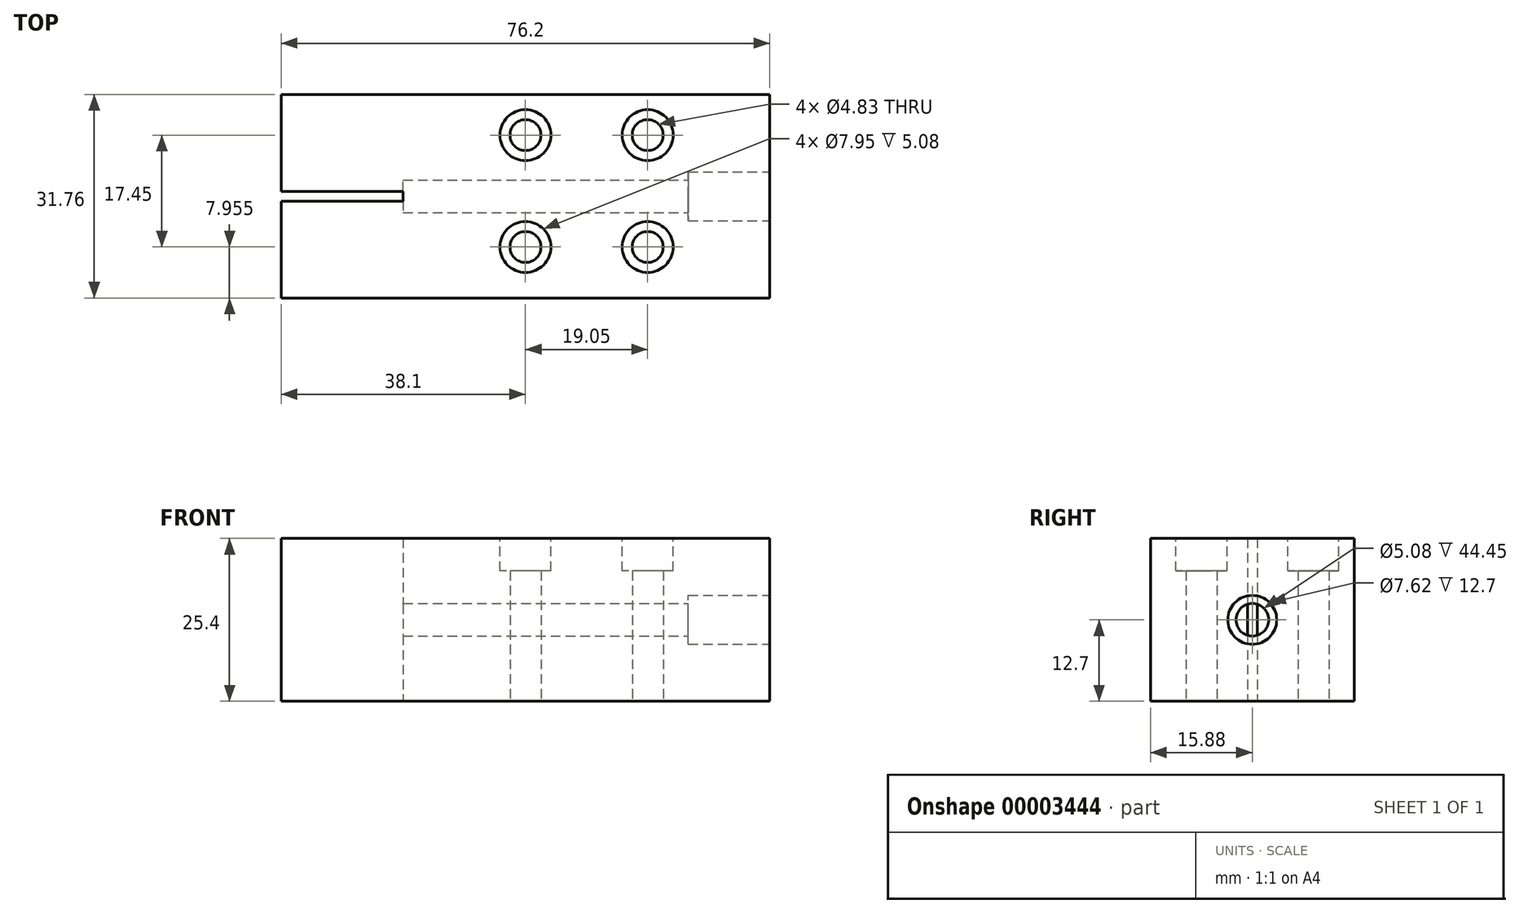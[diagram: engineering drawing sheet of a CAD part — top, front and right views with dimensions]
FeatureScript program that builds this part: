
annotation { "Feature Type Name" : "Feature", "Feature Type Description" : "" }
export const myFeature = defineFeature(function(context is Context, id is Id, definition is map)
    precondition{}
    {
        {
            var Q0;
            Q0=qCreatedBy(makeId("Top.planeOp"),FACE);
            var sketch = newSketch(context, id + "F0", { "sketchPlane" : qUnion([Q0])});
            skLineSegment(sketch, "E0.rect.bottom", {"start": v(-38.1, 15.88) * mm, "end": v(38.1, 15.88) * mm});
            skLineSegment(sketch, "E0.rect.top", {"start": v(-38.1, -15.88) * mm, "end": v(38.1, -15.88) * mm});
            skLineSegment(sketch, "E0.rect.right", {"start": v(38.1, 15.88) * mm, "end": v(38.1, -15.87) * mm});
            skPoint(sketch, "E0.rect.middle", {"position": v(0, 0) * mm});
            skLineSegment(sketch, "E1.rect.bottom", {"start": v(-38.1, 0.76) * mm, "end": v(-19.05, 0.76) * mm});
            skLineSegment(sketch, "E1.rect.top", {"start": v(-38.1, -0.76) * mm, "end": v(-19.05, -0.76) * mm});
            skLineSegment(sketch, "E1.rect.right", {"start": v(-19.05, 0.76) * mm, "end": v(-19.05, -0.76) * mm});
            skPoint(sketch, "E1.rect.middle", {"position": v(-28.58, 0) * mm});
            skLineSegment(sketch, "E2", {"start": v(-38.1, -0.76) * mm, "end": v(-38.1, -15.88) * mm});
            skLineSegment(sketch, "E3", {"start": v(-38.1, 15.88) * mm, "end": v(-38.1, 0.76) * mm});
            skCircle(sketch, "E4", {"center": v(0, 9.53) * mm, "radius": 2.41 * mm});
            skCircle(sketch, "E5", {"center": v(0, -7.92) * mm, "radius": 2.41 * mm});
            skCircle(sketch, "E6", {"center": v(19.05, -7.92) * mm, "radius": 2.41 * mm});
            skCircle(sketch, "E7", {"center": v(19.05, 9.53) * mm, "radius": 2.41 * mm});
            skSolve(sketch);
        }
        {
            var Q0;
            Q0=makeQuery(id+"F0.imprint","IMPRINT",FACE,{"disambiguationData":[TD([[makeQuery(id+"F0.imprint","IMPRINT",EDGE,{"derivedFrom":sQuery(id+"F0.wireOp",EDGE,"E0.rect.bottom")}),-1.0]])]});
            extrude(context, id + "F1", {"entities" : qUnion([Q0]), "depth" : 25.4 * mm});
        }
        {
            var Q0;
            Q0=makeQuery(id+"F1.opExtrude","SWEPT_FACE",FACE,{"disambiguationData":[OSD([sQuery(id+"F0.wireOp",EDGE,"E0.rect.right")])]});
            var sketch = newSketch(context, id + "F2", { "sketchPlane" : qUnion([Q0])});
            skCircle(sketch, "E8", {"center": v(0, 12.7) * mm, "radius": 2.54 * mm});
            skCircle(sketch, "E9", {"center": v(0, 12.7) * mm, "radius": 3.81 * mm});
            skSolve(sketch);
        }
        {
            var Q0;
            Q0=makeQuery(id+"F2.imprint","IMPRINT",FACE,{"disambiguationData":[TD([[makeQuery(id+"F2.imprint","IMPRINT",EDGE,{"derivedFrom":sQuery(id+"F2.wireOp",EDGE,"E8")}),1.0]])]});
            extrude(context, id + "F3", {"entities" : qUnion([Q0]), "operationType" : NewBodyOperationType.REMOVE, "oppositeDirection" : true, "depth" : 57.15 * mm});
        }
        {
            var Q0;
            Q0=makeQuery(id+"F2.imprint","IMPRINT",FACE,{"disambiguationData":[TD([[makeQuery(id+"F2.imprint","IMPRINT",EDGE,{"derivedFrom":sQuery(id+"F2.wireOp",EDGE,"E8")}),-1.0]])]});
            extrude(context, id + "F4", {"entities" : qUnion([Q0]), "operationType" : NewBodyOperationType.REMOVE, "oppositeDirection" : true, "depth" : 12.7 * mm});
        }
        {
            var Q0;
            Q0=makeQuery(id+"F1.opExtrude","CAP_FACE",FACE,{"disambiguationData":[OSD([sQuery(id+"F0.wireOp",EDGE,"E0.rect.bottom"),sQuery(id+"F0.wireOp",EDGE,"E0.rect.top"),sQuery(id+"F0.wireOp",EDGE,"E0.rect.right"),sQuery(id+"F0.wireOp",EDGE,"E1.rect.bottom"),sQuery(id+"F0.wireOp",EDGE,"E1.rect.top"),sQuery(id+"F0.wireOp",EDGE,"E1.rect.right"),sQuery(id+"F0.wireOp",EDGE,"E2"),sQuery(id+"F0.wireOp",EDGE,"E3"),sQuery(id+"F0.wireOp",EDGE,"E4"),sQuery(id+"F0.wireOp",EDGE,"E5"),sQuery(id+"F0.wireOp",EDGE,"E6"),sQuery(id+"F0.wireOp",EDGE,"E7")])],"isStart":false});
            var sketch = newSketch(context, id + "F5", { "sketchPlane" : qUnion([Q0])});
            skCircle(sketch, "E10", {"center": v(0, 9.53) * mm, "radius": 3.98 * mm});
            skCircle(sketch, "E11", {"center": v(19.05, 9.53) * mm, "radius": 3.98 * mm});
            skCircle(sketch, "E12", {"center": v(19.05, -7.92) * mm, "radius": 3.98 * mm});
            skCircle(sketch, "E13", {"center": v(0, -7.92) * mm, "radius": 3.98 * mm});
            skSolve(sketch);
        }
        {
            var Q0;
            Q0=makeQuery(id+"F5.imprint","IMPRINT",FACE,{"disambiguationData":[TD([[makeQuery(id+"F5.imprint","IMPRINT",EDGE,{"derivedFrom":sQuery(id+"F5.wireOp",EDGE,"E10")}),1.0]])]});
            var Q1;
            Q1=makeQuery(id+"F5.imprint","IMPRINT",FACE,{"disambiguationData":[TD([[makeQuery(id+"F5.imprint","IMPRINT",EDGE,{"derivedFrom":sQuery(id+"F5.wireOp",EDGE,"E11")}),1.0]])]});
            var Q2;
            Q2=makeQuery(id+"F5.imprint","IMPRINT",FACE,{"disambiguationData":[TD([[makeQuery(id+"F5.imprint","IMPRINT",EDGE,{"derivedFrom":sQuery(id+"F5.wireOp",EDGE,"E12")}),1.0]])]});
            var Q3;
            Q3=makeQuery(id+"F5.imprint","IMPRINT",FACE,{"disambiguationData":[TD([[makeQuery(id+"F5.imprint","IMPRINT",EDGE,{"derivedFrom":sQuery(id+"F5.wireOp",EDGE,"E13")}),1.0]])]});
            extrude(context, id + "F6", {"entities" : qUnion([Q0, Q1, Q2, Q3]), "operationType" : NewBodyOperationType.REMOVE, "oppositeDirection" : true, "depth" : 5.08 * mm});
        }
    });
